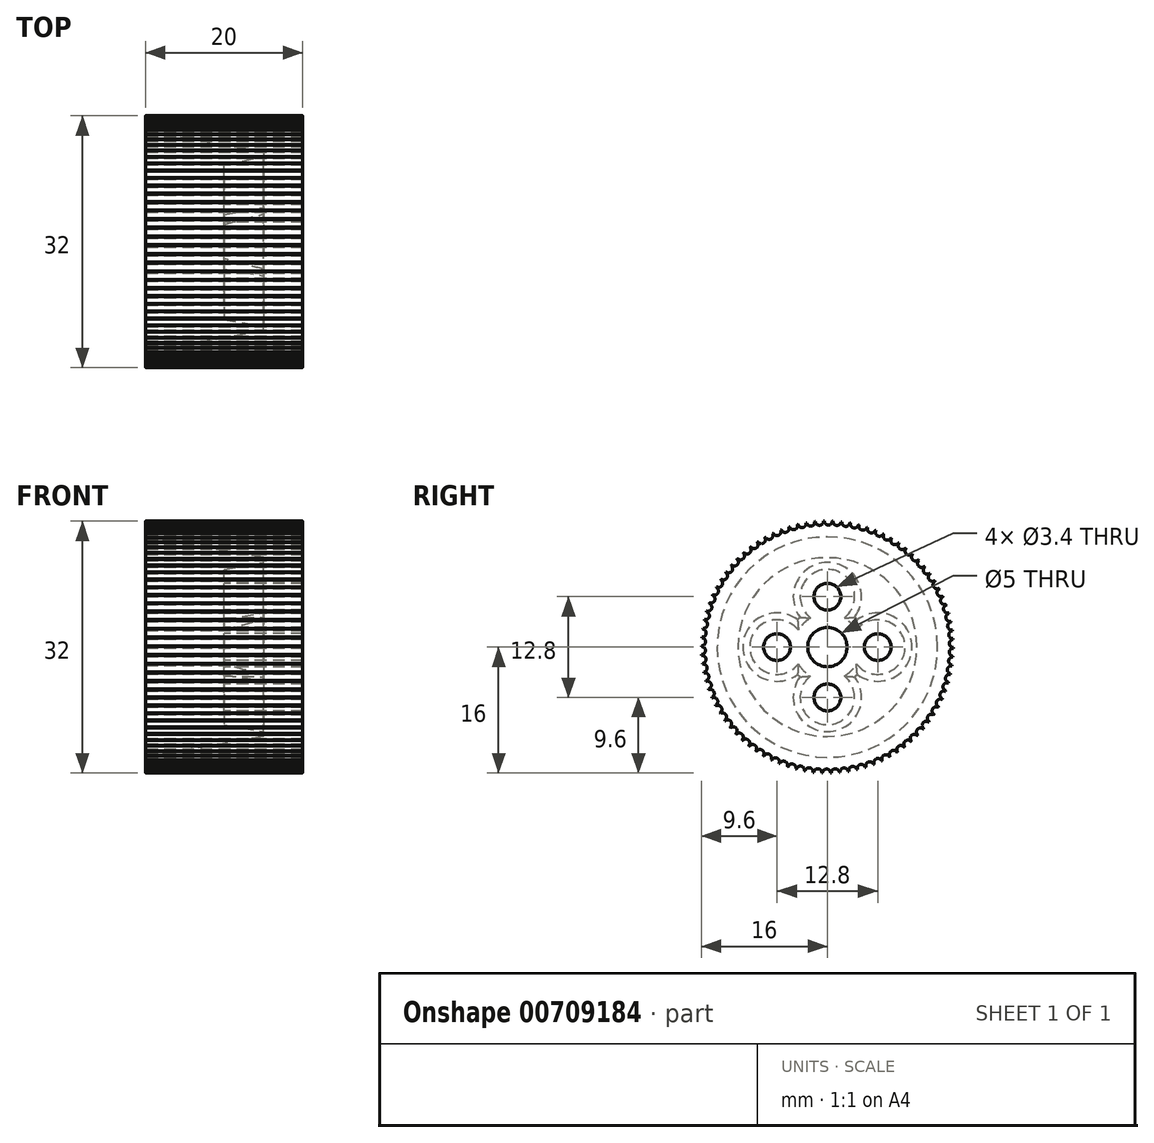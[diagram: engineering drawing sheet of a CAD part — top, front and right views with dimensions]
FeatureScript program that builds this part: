
annotation { "Feature Type Name" : "Feature", "Feature Type Description" : "" }
export const myFeature = defineFeature(function(context is Context, id is Id, definition is map)
    precondition{}
    {
        {
            var Q0;
            Q0=qCreatedBy(makeId("Right.planeOp"),FACE);
            var sketch = newSketch(context, id + "F0", { "sketchPlane" : qUnion([Q0])});
            skCircle(sketch, "E0", {"center": v(0, 0) * mm, "radius": 16 * mm});
            skCircle(sketch, "E1", {"center": v(0, 0) * mm, "radius": 2.5 * mm});
            skCircle(sketch, "E2", {"center": v(0, 6.4) * mm, "radius": 1.7 * mm});
            skCircle(sketch, "E3", {"center": v(6.4, 0) * mm, "radius": 1.7 * mm});
            skCircle(sketch, "E4", {"center": v(0, -6.4) * mm, "radius": 1.7 * mm});
            skCircle(sketch, "E5", {"center": v(-6.4, 0) * mm, "radius": 1.7 * mm});
            skCircle(sketch, "E6", {"center": v(0, 0) * mm, "radius": 14 * mm});
            skCircle(sketch, "E7", {"center": v(0.1, 16) * mm, "radius": 0.5 * mm});
            skCircle(sketch, "E8", {"center": v(0, 0) * mm, "radius": 11.03 * mm});
            skSolve(sketch);
        }
        {
            var Q0;
            Q0=makeQuery(id+"F0.imprint","IMPRINT",FACE,{"disambiguationData":[TD([[makeQuery(id+"F0.imprint","IMPRINT",EDGE,{"derivedFrom":sQuery(id+"F0.wireOp",EDGE,"E0")}),1.0]])]});
            var Q1;
            Q1=makeQuery(id+"F0.imprint","IMPRINT",FACE,{"disambiguationData":[TD([[makeQuery(id+"F0.imprint","IMPRINT",EDGE,{"derivedFrom":sQuery(id+"F0.wireOp",EDGE,"E6")}),1.0]])]});
            var Q2;
            Q2=makeQuery(id+"F0.imprint","IMPRINT",FACE,{"disambiguationData":[TD([[makeQuery(id+"F0.imprint","IMPRINT",EDGE,{"derivedFrom":sQuery(id+"F0.wireOp",EDGE,"E1")}),-1.0]])]});
            var Q3;
            Q3=makeQuery(id+"F0.imprint","IMPRINT",FACE,{"disambiguationData":[TD([[makeQuery(id+"F0.imprint","IMPRINT",EDGE,{"derivedFrom":sQuery(id+"F0.wireOp",EDGE,"E6")}),-1.0]])]});
            extrude(context, id + "F1", {"entities" : qUnion([Q0, Q1, Q2, Q3]), "depth" : 20 * mm, "offsetDistance" : 25 * mm});
        }
        {
            var Q0;
            Q0=makeQuery(id+"F0.imprint","IMPRINT",FACE,{"disambiguationData":[TD([[makeQuery(id+"F0.imprint","IMPRINT",EDGE,{"derivedFrom":sQuery(id+"F0.wireOp",EDGE,"E1")}),-1.0]])]});
            var Q1;
            Q1=makeQuery(id+"F0.imprint","IMPRINT",FACE,{"disambiguationData":[TD([[makeQuery(id+"F0.imprint","IMPRINT",EDGE,{"derivedFrom":sQuery(id+"F0.wireOp",EDGE,"E6")}),1.0]])]});
            extrude(context, id + "F2", {"entities" : qUnion([Q0, Q1]), "operationType" : NewBodyOperationType.REMOVE, "depth" : 15 * mm, "offsetDistance" : 25 * mm, "hasDraft" : true, "draftAngle" : 10 * degree, "draftPullDirection" : true});
        }
        {
            var Q0;
            Q0=makeQuery(id+"F0.imprint","IMPRINT",FACE,{"disambiguationData":[TD([[makeQuery(id+"F0.imprint","IMPRINT",EDGE,{"derivedFrom":sQuery(id+"F0.wireOp",EDGE,"E1")}),-1.0]])]});
            var sketch = newSketch(context, id + "F3", { "sketchPlane" : qUnion([Q0])});
            skSolve(sketch);
        }
        {
            var Q0;
            Q0=makeQuery(id+"F3.imprint","IMPRINT",FACE,{"disambiguationData":[TD([[makeQuery(id+"F3.imprint","IMPRINT",EDGE,{"derivedFrom":sQuery(id+"F3.wireOp",EDGE,"5rjhHb7A-Vbg1-qnA1-kewo-VjsLxLBDlHtx")}),1.0]])]});
            var Q1;
            Q1=makeQuery(id+"F3.imprint","IMPRINT",FACE,{"disambiguationData":[TD([[makeQuery(id+"F3.imprint","IMPRINT",EDGE,{"derivedFrom":makeQuery(id+"F0.imprint","IMPRINT",EDGE,{"derivedFrom":sQuery(id+"F0.wireOp",EDGE,"E1")})}),-1.0]])]});
            extrude(context, id + "F4", {"entities" : qUnion([Q0, Q1]), "operationType" : NewBodyOperationType.REMOVE, "depth" : 10 * mm, "offsetDistance" : 25 * mm});
        }
        {
            var Q0;
            {var subQ0=sQuery(id+"F0.wireOp",EDGE,"E7");var subQ1=sQuery(id+"F0.wireOp",EDGE,"E0");var subQ2=makeQuery(id+"F0.imprint","INTERSECT",VERTEX,{"disambiguationData":[OD(0.0)],"derivedFrom":[subQ1,subQ0]});Q0=makeQuery(id+"F0.imprint","IMPRINT",FACE,{"disambiguationData":[TD([[makeQuery(id+"F0.imprint","IMPRINT",EDGE,{"disambiguationData":[TD([[subQ2,1.0]])],"derivedFrom":subQ1}),1.0]])]});}
            var Q1;
            {var subQ0=sQuery(id+"F0.wireOp",EDGE,"E7");var subQ1=sQuery(id+"F0.wireOp",EDGE,"E0");var subQ2=makeQuery(id+"F0.imprint","INTERSECT",VERTEX,{"disambiguationData":[OD(0.0)],"derivedFrom":[subQ1,subQ0]});Q1=makeQuery(id+"F0.imprint","IMPRINT",FACE,{"disambiguationData":[TD([[makeQuery(id+"F0.imprint","IMPRINT",EDGE,{"disambiguationData":[TD([[subQ2,1.0]])],"derivedFrom":subQ1}),-1.0]])]});}
            extrude(context, id + "F5", {"entities" : qUnion([Q0, Q1]), "depth" : 21 * mm, "offsetDistance" : 25 * mm, "hasSecondDirection" : true, "secondDirectionOppositeDirection" : true, "secondDirectionDepth" : 1 * mm});
        }
        {
            var Q0;
            Q0=qCreatedBy(makeId("Front.planeOp"),FACE);
            var sketch = newSketch(context, id + "F6", { "sketchPlane" : qUnion([Q0])});
            skLineSegment(sketch, "E9", {"start": v(41, 0) * mm, "end": v(-25.31, 0) * mm});
            skSolve(sketch);
        }
        {
            var Q0;
            Q0=makeQuery(id+"F5.opExtrude","SWEPT_BODY",BODY,{"disambiguationData":[OSD([sQuery(id+"F0.wireOp",EDGE,"E7")])]});
            var Q1;
            Q1=sQuery(id+"F6.wireOp",EDGE,"E9");
            circularPattern(context, id + "F7", {"operationType" : NewBodyOperationType.REMOVE, "entities" : qUnion([Q0]), "axis" : qUnion([Q1]), "angle" : 360 * degree, "instanceCount" : 90, "equalSpace" : true});
        }
    });
